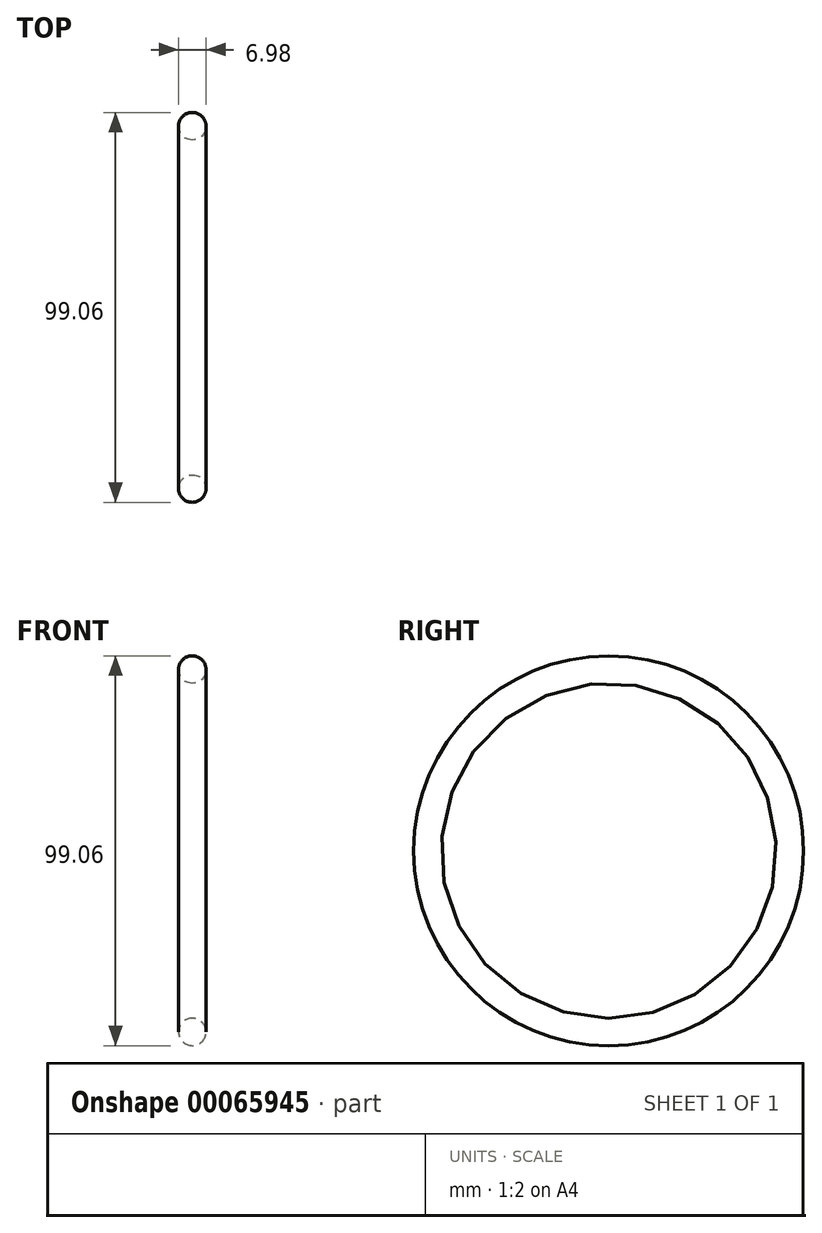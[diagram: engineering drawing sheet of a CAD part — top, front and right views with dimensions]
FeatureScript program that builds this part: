
annotation { "Feature Type Name" : "Feature", "Feature Type Description" : "" }
export const myFeature = defineFeature(function(context is Context, id is Id, definition is map)
    precondition{}
    {
        {
            var Q0;
            Q0=qCreatedBy(makeId("Front.planeOp"),FACE);
            var sketch = newSketch(context, id + "F0", { "sketchPlane" : qUnion([Q0])});
            skLineSegment(sketch, "E0", {"start": v(0, 0) * mm, "end": v(-6.06, 0) * mm, "construction": true});
            skCircle(sketch, "E1", {"center": v(0, 46.04) * mm, "radius": 3.5 * mm});
            skSolve(sketch);
        }
        {
            var Q0;
            Q0=makeQuery(id+"F0.imprint","IMPRINT",FACE,{"disambiguationData":[TD([[makeQuery(id+"F0.imprint","IMPRINT",EDGE,{"derivedFrom":sQuery(id+"F0.wireOp",EDGE,"E1")}),1.0]])]});
            var Q1;
            Q1=sQuery(id+"F0.wireOp",EDGE,"E0");
            revolve(context, id + "F1", {"entities" : qUnion([Q0]), "axis" : qUnion([Q1]), "revolveType" : RevolveType.FULL});
        }
    });
